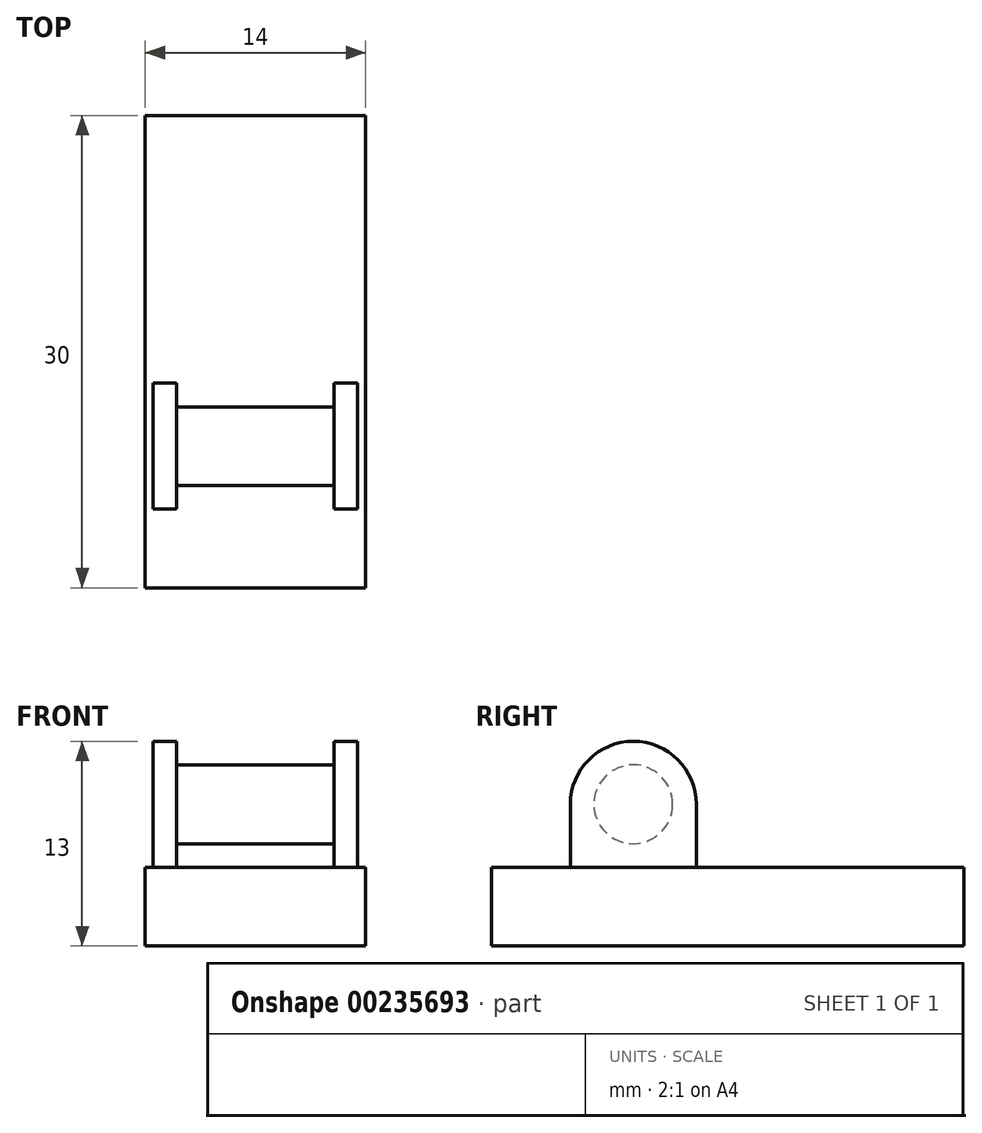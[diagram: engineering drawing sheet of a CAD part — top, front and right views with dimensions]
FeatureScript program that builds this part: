
annotation { "Feature Type Name" : "Feature", "Feature Type Description" : "" }
export const myFeature = defineFeature(function(context is Context, id is Id, definition is map)
    precondition{}
    {
        {
            var Q0;
            Q0=qCreatedBy(makeId("Front.planeOp"),FACE);
            var sketch = newSketch(context, id + "F0", { "sketchPlane" : qUnion([Q0])});
            skLineSegment(sketch, "E0.bottom", {"start": v(0, 0) * mm, "end": v(-14, 0) * mm});
            skLineSegment(sketch, "E0.top", {"start": v(0, 5) * mm, "end": v(-0.5, 5) * mm});
            skLineSegment(sketch, "E0.left", {"start": v(0, 0) * mm, "end": v(0, 5) * mm});
            skLineSegment(sketch, "E0.right", {"start": v(-14, 0) * mm, "end": v(-14, 5) * mm});
            skLineSegment(sketch, "E1.top", {"start": v(-13.5, 13) * mm, "end": v(-12, 13) * mm, "construction": true});
            skLineSegment(sketch, "E1.left", {"start": v(-13.5, 5) * mm, "end": v(-13.5, 13) * mm, "construction": true});
            skLineSegment(sketch, "E1.right", {"start": v(-12, 5) * mm, "end": v(-12, 13) * mm, "construction": true});
            skLineSegment(sketch, "E2.top", {"start": v(-0.5, 13) * mm, "end": v(-2, 13) * mm, "construction": true});
            skLineSegment(sketch, "E2.left", {"start": v(-0.5, 5) * mm, "end": v(-0.5, 13) * mm, "construction": true});
            skLineSegment(sketch, "E2.right", {"start": v(-2, 5) * mm, "end": v(-2, 13) * mm, "construction": true});
            skLineSegment(sketch, "E3.trimOffspring", {"start": v(-13.5, 5) * mm, "end": v(-14, 5) * mm});
            skLineSegment(sketch, "E4.trimOffspring", {"start": v(-2, 5) * mm, "end": v(-12, 5) * mm});
            skLineSegment(sketch, "E5", {"start": v(-13.5, 5) * mm, "end": v(-12, 5) * mm});
            skLineSegment(sketch, "E6", {"start": v(-2, 5) * mm, "end": v(-0.5, 5) * mm});
            skSolve(sketch);
        }
        {
            var Q0;
            Q0=makeQuery(id+"F0.imprint","IMPRINT",FACE,{"disambiguationData":[TD([[makeQuery(id+"F0.imprint","IMPRINT",EDGE,{"derivedFrom":sQuery(id+"F0.wireOp",EDGE,"E0.bottom")}),-1.0]])]});
            extrude(context, id + "F1", {"entities" : qUnion([Q0]), "depth" : 30 * mm});
        }
        {
            var Q0;
            Q0=qCreatedBy(makeId("Front.planeOp"),FACE);
            cPlane(context, id + "F2", {"entities" : qUnion([Q0]), "cplaneType" : CPlaneType.OFFSET, "offset" : 25 * mm, "width" : 150 * mm, "height" : 150 * mm});
        }
        {
            var Q0;
            Q0=qCreatedBy(id+"F2.planeOp",FACE);
            var sketch = newSketch(context, id + "F3", { "sketchPlane" : qUnion([Q0])});
            skLineSegment(sketch, "E7.0", {"start": v(-13.5, 5) * mm, "end": v(-13.5, 13) * mm});
            skLineSegment(sketch, "E8.0", {"start": v(-13.5, 13) * mm, "end": v(-12, 13) * mm});
            skLineSegment(sketch, "E9.0", {"start": v(-12, 5) * mm, "end": v(-12, 13) * mm});
            skLineSegment(sketch, "E10.0", {"start": v(-0.5, 13) * mm, "end": v(-2, 13) * mm});
            skLineSegment(sketch, "E11.0", {"start": v(-2, 5) * mm, "end": v(-2, 13) * mm});
            skLineSegment(sketch, "E12.0", {"start": v(-0.5, 5) * mm, "end": v(-0.5, 13) * mm});
            skLineSegment(sketch, "E13", {"start": v(-13.5, 5) * mm, "end": v(-12, 5) * mm});
            skLineSegment(sketch, "E14", {"start": v(-2, 5) * mm, "end": v(-0.5, 5) * mm});
            skSolve(sketch);
        }
        {
            var Q0;
            Q0=makeQuery(id+"F3.imprint","IMPRINT",FACE,{"disambiguationData":[TD([[makeQuery(id+"F3.imprint","IMPRINT",EDGE,{"derivedFrom":sQuery(id+"F3.wireOp",EDGE,"E7.0")}),-1.0]])]});
            var Q1;
            Q1=makeQuery(id+"F3.imprint","IMPRINT",FACE,{"disambiguationData":[TD([[makeQuery(id+"F3.imprint","IMPRINT",EDGE,{"derivedFrom":sQuery(id+"F3.wireOp",EDGE,"E10.0")}),1.0]])]});
            extrude(context, id + "F4", {"entities" : qUnion([Q0, Q1]), "operationType" : NewBodyOperationType.ADD, "oppositeDirection" : true, "depth" : 8 * mm});
        }
        {
            var Q0;
            Q0=makeQuery(id+"F4.opExtrude","SWEPT_FACE",FACE,{"disambiguationData":[OSD([sQuery(id+"F3.wireOp",EDGE,"E12.0")])]});
            var sketch = newSketch(context, id + "F5", { "sketchPlane" : qUnion([Q0])});
            skCircle(sketch, "E15", {"center": v(-21, 9) * mm, "radius": 2.5 * mm});
            skSolve(sketch);
        }
        {
            var Q0;
            Q0 = qSketchRegion(id + "F5", true);
            var Q1;
            Q1=makeQuery(id+"F4.opExtrude","SWEPT_FACE",FACE,{"disambiguationData":[OSD([sQuery(id+"F3.wireOp",EDGE,"E7.0")])]});
            extrude(context, id + "F6", {"entities" : qUnion([Q0]), "operationType" : NewBodyOperationType.ADD, "endBound" : BoundingType.UP_TO_SURFACE, "oppositeDirection" : true, "endBoundEntityFace" : qUnion([Q1]), "depth" : 25 * mm});
        }
        {
            var Q0;
            Q0=makeQuery(id+"F4.opExtrude","CAP_EDGE",EDGE,{"disambiguationData":[OSD([sQuery(id+"F3.wireOp",EDGE,"E10.0")])],"isStart":false});
            var Q1;
            Q1=makeQuery(id+"F4.opExtrude","CAP_EDGE",EDGE,{"disambiguationData":[OSD([sQuery(id+"F3.wireOp",EDGE,"E10.0")])],"isStart":true});
            var Q2;
            Q2=makeQuery(id+"F4.opExtrude","CAP_EDGE",EDGE,{"disambiguationData":[OSD([sQuery(id+"F3.wireOp",EDGE,"E8.0")])],"isStart":false});
            var Q3;
            Q3=makeQuery(id+"F4.opExtrude","CAP_EDGE",EDGE,{"disambiguationData":[OSD([sQuery(id+"F3.wireOp",EDGE,"E8.0")])],"isStart":true});
            fillet(context, id + "F7", {"entities" : qUnion([Q0, Q1, Q2, Q3]), "radius" : 4 * mm, "tangentPropagation" : true, "allowEdgeOverflow" : false});
        }
    });
